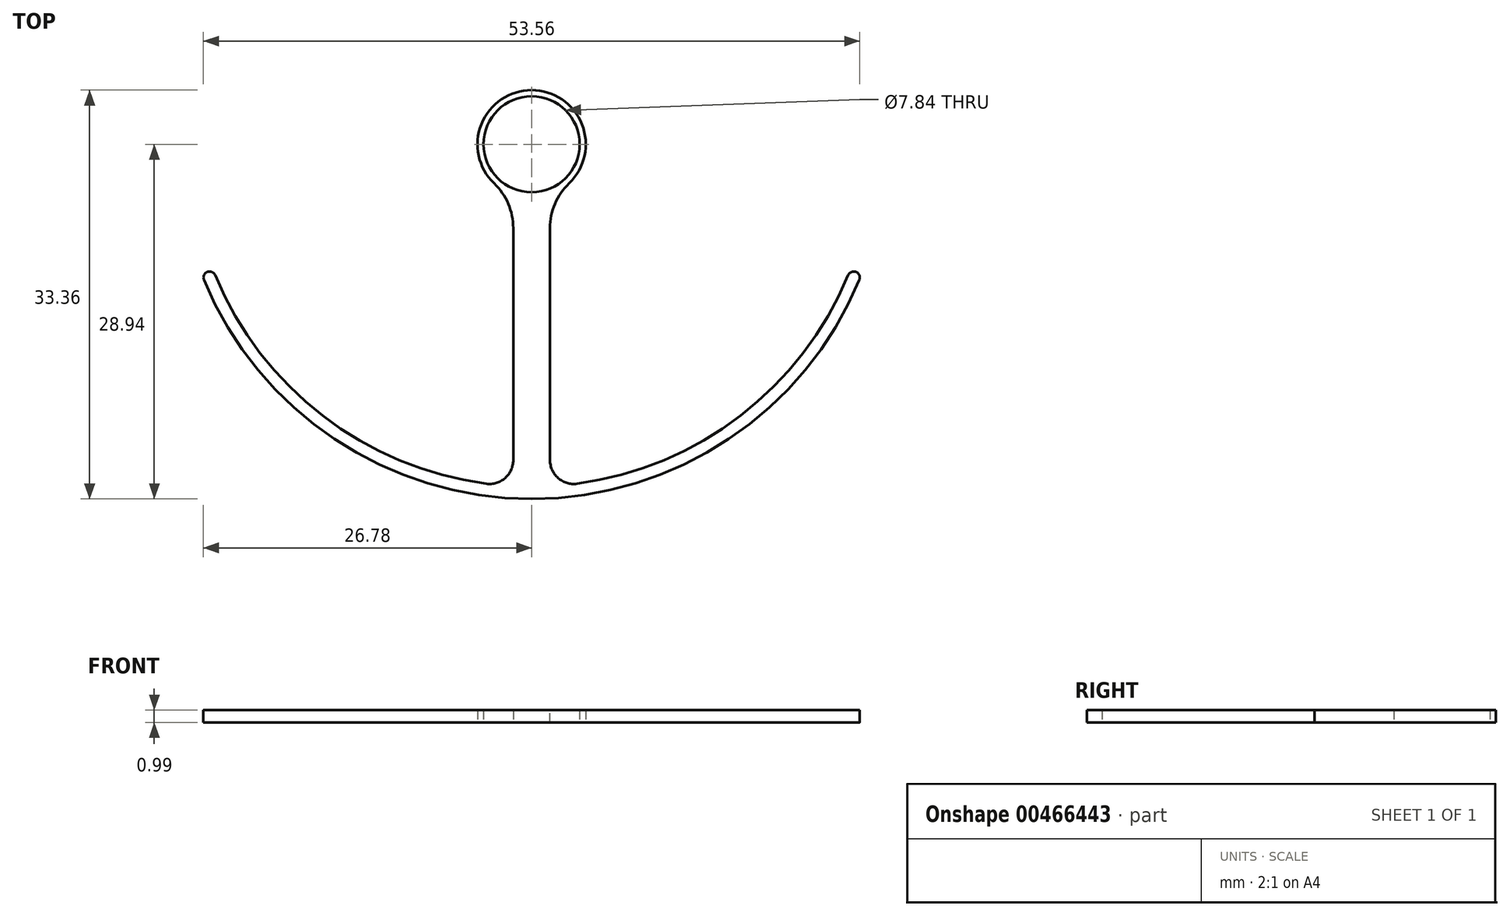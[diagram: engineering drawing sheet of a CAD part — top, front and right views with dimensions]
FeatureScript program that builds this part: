
annotation { "Feature Type Name" : "Feature", "Feature Type Description" : "" }
export const myFeature = defineFeature(function(context is Context, id is Id, definition is map)
    precondition{}
    {
        {
            var Q0;
            Q0=qCreatedBy(makeId("Top.planeOp"),FACE);
            var sketch = newSketch(context, id + "F0", { "sketchPlane" : qUnion([Q0])});
            skCircle(sketch, "E0", {"center": v(0, 0) * mm, "radius": 3.92 * mm});
            skArc(sketch, "E1", {"start": v(1.5, -4.16) * mm, "mid": v(0, 4.42) * mm, "end": v(-1.5, -4.16) * mm});
            skCircle(sketch, "E2", {"center": v(0, 0) * mm, "radius": 28.5 * mm, "construction": true});
            skLineSegment(sketch, "E3.top", {"start": v(-1.5, -28.46) * mm, "end": v(1.5, -28.46) * mm});
            skLineSegment(sketch, "E3.left", {"start": v(-1.5, -4.16) * mm, "end": v(-1.5, -28.46) * mm});
            skLineSegment(sketch, "E3.right", {"start": v(1.5, -4.16) * mm, "end": v(1.5, -28.46) * mm});
            skSolve(sketch);
        }
        {
            var Q0;
            Q0=qCreatedBy(makeId("Top.planeOp"),FACE);
            var sketch = newSketch(context, id + "F1", { "sketchPlane" : qUnion([Q0])});
            skArc(sketch, "E4", {"start": v(26.47, -10.43) * mm, "mid": v(0, 28.45) * mm, "end": v(-26.47, -10.43) * mm});
            skArc(sketch, "E5", {"start": v(26.74, -11.08) * mm, "mid": v(26.47, -10.43) * mm, "end": v(25.82, -10.7) * mm});
            skLineSegment(sketch, "E6", {"start": v(0, 0) * mm, "end": v(39.5, -16.36) * mm, "construction": true});
            skLineSegment(sketch, "E7", {"start": v(0, 0) * mm, "end": v(-39.5, -16.36) * mm, "construction": true});
            skArc(sketch, "E8.MirrorC", {"start": v(-26.74, -11.08) * mm, "mid": v(-26.47, -10.43) * mm, "end": v(-25.82, -10.7) * mm});
            skArc(sketch, "E9", {"start": v(-25.82, -10.7) * mm, "mid": v(0, -27.95) * mm, "end": v(25.82, -10.7) * mm});
            skArc(sketch, "E10", {"start": v(-26.74, -11.08) * mm, "mid": v(0, -28.94) * mm, "end": v(26.74, -11.08) * mm});
            skSolve(sketch);
        }
        {
            var Q0;
            Q0=makeQuery(id+"F0.imprint","IMPRINT",FACE,{"disambiguationData":[TD([[makeQuery(id+"F0.imprint","IMPRINT",EDGE,{"derivedFrom":sQuery(id+"F0.wireOp",EDGE,"E0")}),-1.0]])]});
            extrude(context, id + "F2", {"entities" : qUnion([Q0]), "depth" : 1 * mm, "offsetDistance" : 25.4 * mm});
        }
        {
            var Q0;
            Q0=makeQuery(id+"F2.opExtrude","SWEPT_EDGE",EDGE,{"disambiguationData":[OSD([sQuery(id+"F0.wireOp",EDGE,"E1"),sQuery(id+"F0.wireOp",EDGE,"E3.right")])]});
            var Q1;
            Q1=makeQuery(id+"F2.opExtrude","SWEPT_EDGE",EDGE,{"disambiguationData":[OSD([sQuery(id+"F0.wireOp",EDGE,"E1"),sQuery(id+"F0.wireOp",EDGE,"E3.left")])]});
            fillet(context, id + "F3", {"entities" : qUnion([Q0, Q1]), "radius" : 5.08 * mm, "tangentPropagation" : true, "allowEdgeOverflow" : false});
        }
        {
            var Q0;
            {var subQ3=sQuery(id+"F1.wireOp",EDGE,"E9");Q0=makeQuery(id+"F1.imprint","IMPRINT",FACE,{"disambiguationData":[TD([[makeQuery(id+"F1.imprint","IMPRINT",EDGE,{"derivedFrom":subQ3}),-1.0]])]});}
            extrude(context, id + "F4", {"entities" : qUnion([Q0]), "operationType" : NewBodyOperationType.ADD, "depth" : 1 * mm, "offsetDistance" : 25.4 * mm});
        }
        {
            var Q0;
            Q0=makeQuery(id+"F4.boolean.opBoolean","INTERSECT",EDGE,{"derivedFrom":[makeQuery(id+"F2.opExtrude","SWEPT_FACE",FACE,{"disambiguationData":[OSD([sQuery(id+"F0.wireOp",EDGE,"E3.right")])]}),makeQuery(id+"F4.opExtrude","SWEPT_FACE",FACE,{"disambiguationData":[OSD([sQuery(id+"F1.wireOp",EDGE,"E9")])]})]});
            var Q1;
            Q1=makeQuery(id+"F4.boolean.opBoolean","INTERSECT",EDGE,{"derivedFrom":[makeQuery(id+"F2.opExtrude","SWEPT_FACE",FACE,{"disambiguationData":[OSD([sQuery(id+"F0.wireOp",EDGE,"E3.left")])]}),makeQuery(id+"F4.opExtrude","SWEPT_FACE",FACE,{"disambiguationData":[OSD([sQuery(id+"F1.wireOp",EDGE,"E9")])]})]});
            fillet(context, id + "F5", {"entities" : qUnion([Q0, Q1]), "radius" : 1.95 * mm, "tangentPropagation" : true, "allowEdgeOverflow" : false});
        }
    });
